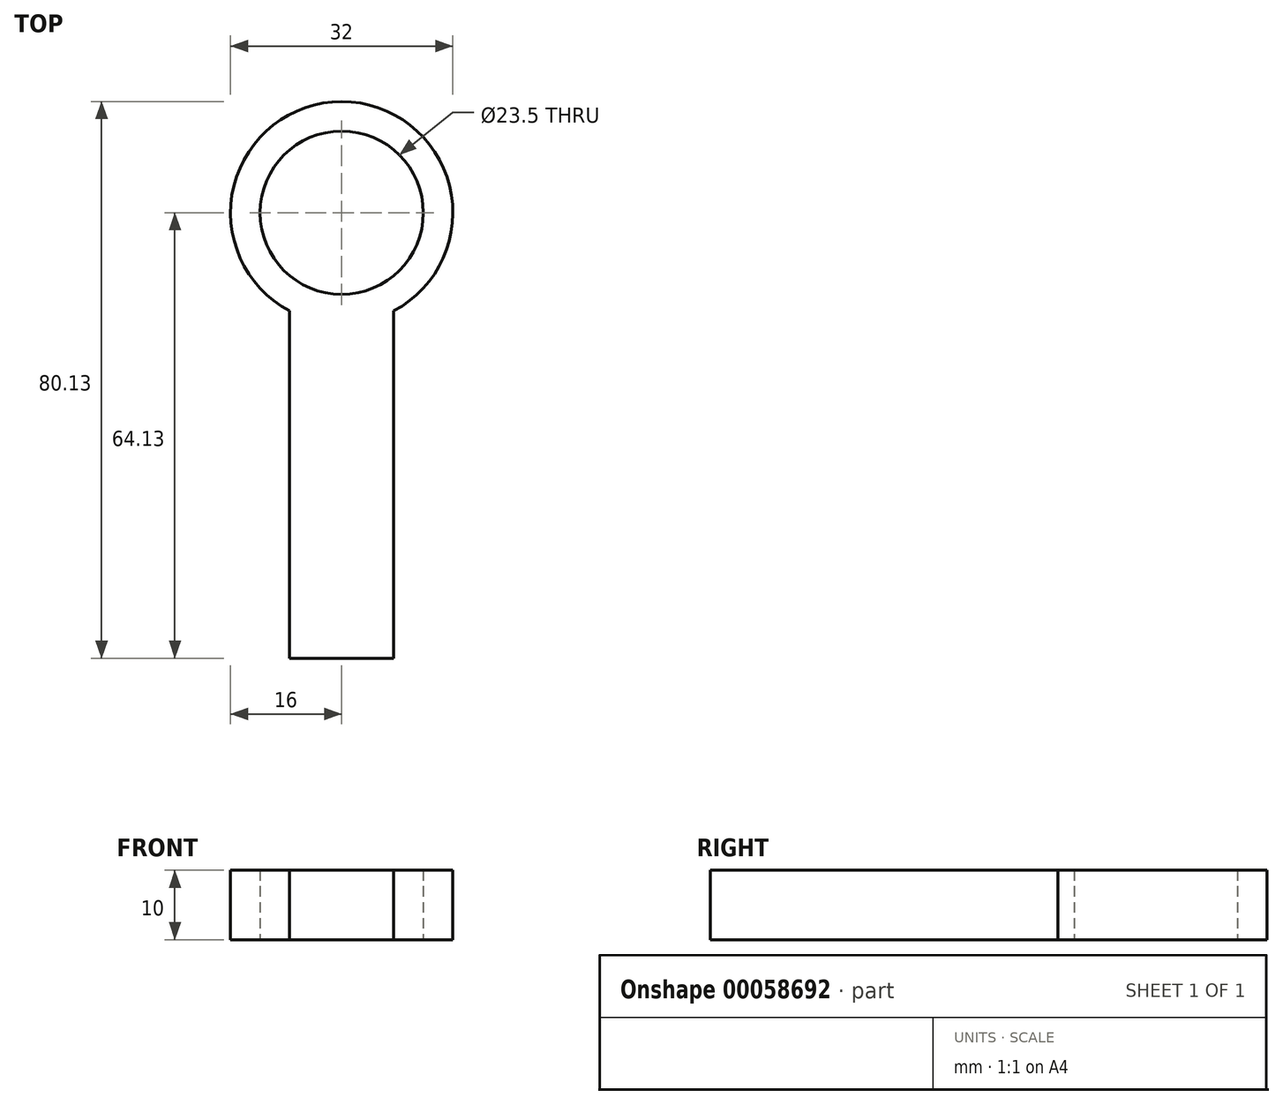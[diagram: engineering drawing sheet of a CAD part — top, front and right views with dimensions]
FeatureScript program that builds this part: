
annotation { "Feature Type Name" : "Feature", "Feature Type Description" : "" }
export const myFeature = defineFeature(function(context is Context, id is Id, definition is map)
    precondition{}
    {
        {
            var Q0;
            Q0=qCreatedBy(makeId("Top.planeOp"),FACE);
            var sketch = newSketch(context, id + "F0", { "sketchPlane" : qUnion([Q0])});
            skArc(sketch, "E0", {"start": v(7.5, -14.13) * mm, "mid": v(0, 16) * mm, "end": v(-7.5, -14.13) * mm});
            skCircle(sketch, "E1", {"center": v(0, 0) * mm, "radius": 11.75 * mm});
            skLineSegment(sketch, "E2.rect.top", {"start": v(-7.5, -64.13) * mm, "end": v(7.5, -64.13) * mm});
            skLineSegment(sketch, "E2.rect.left", {"start": v(-7.5, -14.13) * mm, "end": v(-7.5, -64.13) * mm});
            skLineSegment(sketch, "E2.rect.right", {"start": v(7.5, -14.13) * mm, "end": v(7.5, -64.13) * mm});
            skSolve(sketch);
        }
        {
            var Q0;
            Q0=makeQuery(id+"F0.imprint","IMPRINT",FACE,{"disambiguationData":[TD([[makeQuery(id+"F0.imprint","IMPRINT",EDGE,{"derivedFrom":sQuery(id+"F0.wireOp",EDGE,"E0")}),1.0]])]});
            extrude(context, id + "F1", {"entities" : qUnion([Q0]), "depth" : 10 * mm});
        }
    });
